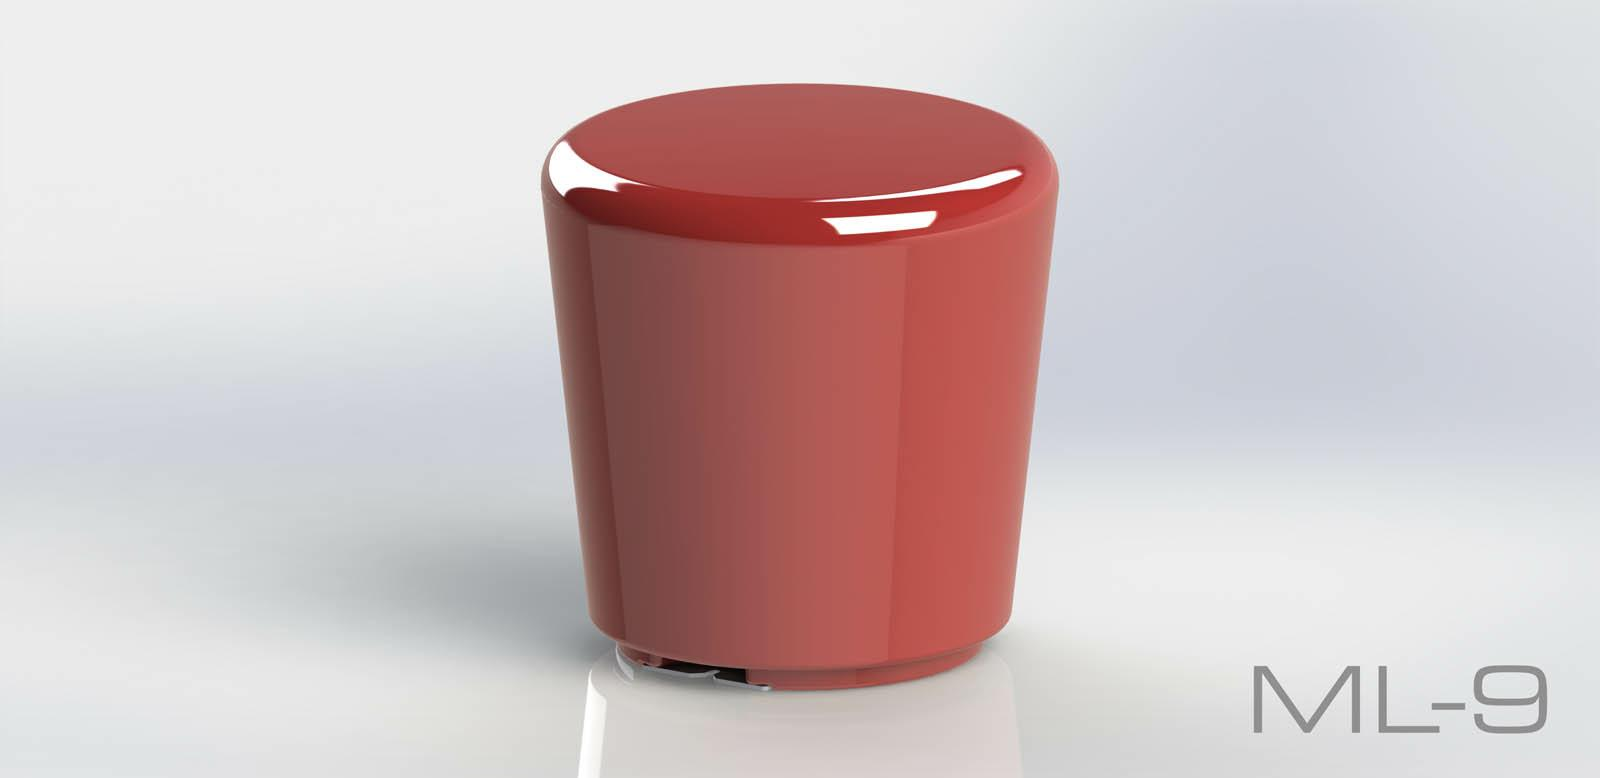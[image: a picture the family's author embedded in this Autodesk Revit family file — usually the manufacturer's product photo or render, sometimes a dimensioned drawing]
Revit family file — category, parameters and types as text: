
# Revit family: Modullaro ML 09
name_source: partatom
category: Furniture
revit_build: Autodesk Revit 2018 (Build: 20190510_1515(x64)
units: mm (PartAtom-declared; Revit-internal decimal feet)

## family parameters
Cut with Voids When Loaded = No
Host = Face
OmniClass Number = 23.40.10.11.14
OmniClass Title = Exterior Seating
Room Calculation Point = No
Shared = No

## types (1)
- Modullaro ML 09
    Default Elevation = 1219 mm
    Height = 500 mm  [stored 1.64042 ft]
    IfcExportAs = IfcFurnishingElement
    Length = 491 mm  [stored 1.61089 ft]
    Manufacturer = Astrini Design
    Material information = Colour choice from RAL colour standard. Customer may inquire about specific request regarding individual order.
    Model = Modullaro ML 09
    Operating temperature = -40°C to 80°C, ( -40°F to 176°F )
    Type Comments = Bench
    Type Image = ML-9.jpg
    URL = https://astrini-design.pl
    Weight (approximately) = 7.00 kg
    Width = 491 mm  [stored 1.61089 ft]

note: [stored X ft] marks values corroborated as IEEE doubles in the binary element streams (Revit-internal decimal feet)
